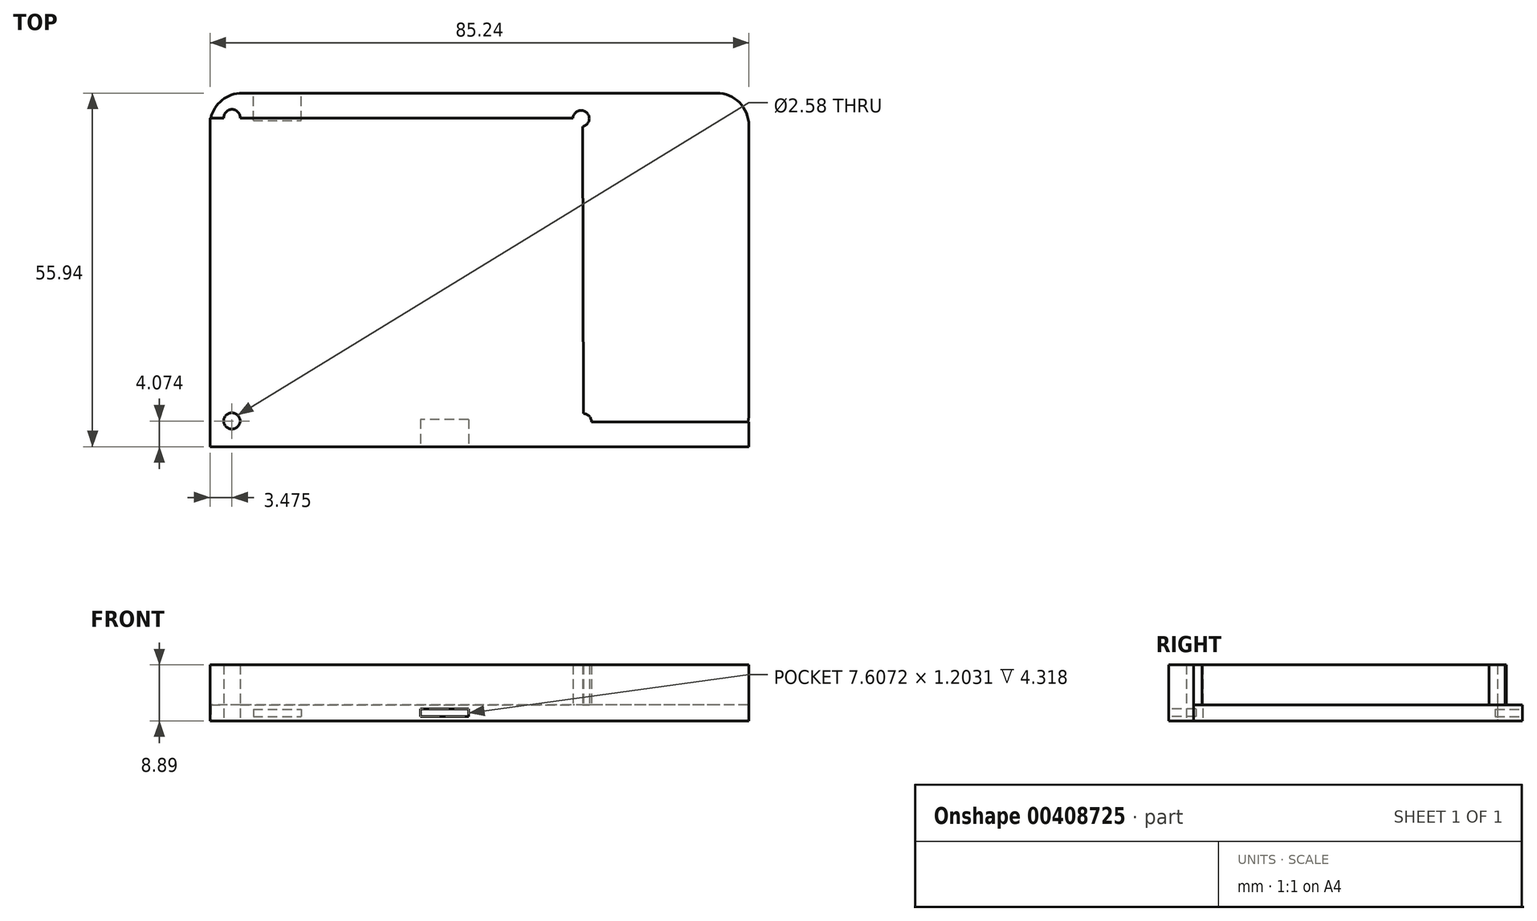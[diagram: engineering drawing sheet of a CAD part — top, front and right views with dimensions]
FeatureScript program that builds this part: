
annotation { "Feature Type Name" : "Feature", "Feature Type Description" : "" }
export const myFeature = defineFeature(function(context is Context, id is Id, definition is map)
    precondition{}
    {
        {
            var Q0;
            Q0=qCreatedBy(makeId("Top.planeOp"),FACE);
            var sketch = newSketch(context, id + "F0", { "sketchPlane" : qUnion([Q0])});
            skLineSegment(sketch, "E0.top", {"start": v(-42.62, -24.03) * mm, "end": v(42.62, -24.03) * mm});
            skLineSegment(sketch, "E0.left", {"start": v(-42.62, 24.03) * mm, "end": v(-42.62, -24.03) * mm});
            skLineSegment(sketch, "E0.right", {"start": v(42.62, 24.03) * mm, "end": v(42.62, -24.03) * mm});
            skPoint(sketch, "E0.middle", {"position": v(0, 0) * mm});
            skLineSegment(sketch, "E1", {"start": v(-42.62, 24.03) * mm, "end": v(-42.62, 27.97) * mm});
            skLineSegment(sketch, "E2.bottom", {"start": v(42.62, 27.97) * mm, "end": v(-42.62, 27.97) * mm});
            skLineSegment(sketch, "E2.top", {"start": v(42.62, -27.97) * mm, "end": v(-42.62, -27.97) * mm});
            skLineSegment(sketch, "E2.left", {"start": v(42.62, 27.97) * mm, "end": v(42.62, -27.97) * mm});
            skLineSegment(sketch, "E2.right", {"start": v(-42.62, 27.97) * mm, "end": v(-42.62, -27.97) * mm});
            skLineSegment(sketch, "E3", {"start": v(16.3, 24.03) * mm, "end": v(-42.62, 24.03) * mm});
            skLineSegment(sketch, "E4", {"start": v(16.3, 24.03) * mm, "end": v(16.46, -24.03) * mm});
            skPoint(sketch, "E5", {"position": v(-39.08, 24.03) * mm});
            skPoint(sketch, "E6", {"position": v(-39.08, -24.03) * mm});
            skPoint(sketch, "E7", {"position": v(16.46, -24.03) * mm});
            skCircle(sketch, "E8", {"center": v(16.43, -24.02) * mm, "radius": 1.3 * mm});
            skCircle(sketch, "E9", {"center": v(-39.13, 24.11) * mm, "radius": 1.3 * mm});
            skCircle(sketch, "E10", {"center": v(-39.15, -23.9) * mm, "radius": 1.3 * mm});
            skCircle(sketch, "E11", {"center": v(16.1, 23.95) * mm, "radius": 1.3 * mm});
            skSolve(sketch);
        }
        {
            var Q0;
            {var subQ3=sQuery(id+"F0.wireOp",EDGE,"E2.bottom");Q0=makeQuery(id+"F0.imprint","IMPRINT",FACE,{"disambiguationData":[TD([[makeQuery(id+"F0.imprint","IMPRINT",EDGE,{"derivedFrom":subQ3}),1.0]])]});}
            var Q1;
            {var subQ6=sQuery(id+"F0.wireOp",EDGE,"E0.top");var subQ10=sQuery(id+"F0.wireOp",EDGE,"E2.right");var subQ11=makeQuery(id+"F0.imprint","INTERSECT",VERTEX,{"derivedFrom":[subQ6,subQ10]});Q1=makeQuery(id+"F0.imprint","IMPRINT",FACE,{"disambiguationData":[TD([[makeQuery(id+"F0.imprint","IMPRINT",EDGE,{"disambiguationData":[TD([[subQ11,-1.0]])],"derivedFrom":subQ6}),1.0]])]});}
            var Q2;
            {var subQ0=sQuery(id+"F0.wireOp",EDGE,"E2.top");Q2=makeQuery(id+"F0.imprint","IMPRINT",FACE,{"disambiguationData":[TD([[makeQuery(id+"F0.imprint","IMPRINT",EDGE,{"derivedFrom":subQ0}),-1.0]])]});}
            extrude(context, id + "F1", {"entities" : qUnion([Q0, Q1, Q2]), "depth" : 2.54 * mm});
        }
        {
            var Q0;
            Q0=makeQuery(id+"F1.opExtrude","SWEPT_EDGE",EDGE,{"disambiguationData":[OSD([sQuery(id+"F0.wireOp",EDGE,"E2.top"),sQuery(id+"F0.wireOp",EDGE,"E2.left")])]});
            var Q1;
            Q1=makeQuery(id+"F1.opExtrude","SWEPT_EDGE",EDGE,{"disambiguationData":[OSD([sQuery(id+"F0.wireOp",EDGE,"E2.top"),sQuery(id+"F0.wireOp",EDGE,"E2.right")])]});
            var Q2;
            Q2=makeQuery(id+"F1.opExtrude","SWEPT_EDGE",EDGE,{"disambiguationData":[OSD([sQuery(id+"F0.wireOp",EDGE,"E2.bottom"),sQuery(id+"F0.wireOp",EDGE,"E2.left")])]});
            var Q3;
            Q3=makeQuery(id+"F1.opExtrude","SWEPT_EDGE",EDGE,{"disambiguationData":[OSD([sQuery(id+"F0.wireOp",EDGE,"E2.bottom"),sQuery(id+"F0.wireOp",EDGE,"E2.right")])]});
            fillet(context, id + "F2", {"entities" : qUnion([Q0, Q1, Q2, Q3]), "radius" : 5.08 * mm, "tangentPropagation" : true, "allowEdgeOverflow" : false});
        }
        {
            var Q0;
            {var subQ0=sQuery(id+"F0.wireOp",EDGE,"E9");var subQ1=sQuery(id+"F0.wireOp",EDGE,"E3");var subQ2=makeQuery(id+"F0.imprint","INTERSECT",VERTEX,{"disambiguationData":[OD(0.0)],"derivedFrom":[subQ1,subQ0]});Q0=makeQuery(id+"F0.imprint","IMPRINT",FACE,{"disambiguationData":[TD([[makeQuery(id+"F0.imprint","IMPRINT",EDGE,{"disambiguationData":[TD([[subQ2,-1.0]])],"derivedFrom":subQ1}),-1.0]])]});}
            var Q1;
            {var subQ0=sQuery(id+"F0.wireOp",EDGE,"E9");var subQ1=sQuery(id+"F0.wireOp",EDGE,"E3");var subQ2=makeQuery(id+"F0.imprint","INTERSECT",VERTEX,{"disambiguationData":[OD(0.0)],"derivedFrom":[subQ1,subQ0]});Q1=makeQuery(id+"F0.imprint","IMPRINT",FACE,{"disambiguationData":[TD([[makeQuery(id+"F0.imprint","IMPRINT",EDGE,{"disambiguationData":[TD([[subQ2,-1.0]])],"derivedFrom":subQ1}),1.0]])]});}
            var Q2;
            {var subQ0=sQuery(id+"F0.wireOp",EDGE,"E10");var subQ1=sQuery(id+"F0.wireOp",EDGE,"E0.top");var subQ2=makeQuery(id+"F0.imprint","INTERSECT",VERTEX,{"disambiguationData":[OD(0.0)],"derivedFrom":[subQ1,subQ0]});Q2=makeQuery(id+"F0.imprint","IMPRINT",FACE,{"disambiguationData":[TD([[makeQuery(id+"F0.imprint","IMPRINT",EDGE,{"disambiguationData":[TD([[subQ2,-1.0]])],"derivedFrom":subQ1}),1.0]])]});}
            var Q3;
            {var subQ0=sQuery(id+"F0.wireOp",EDGE,"E10");var subQ1=sQuery(id+"F0.wireOp",EDGE,"E0.top");var subQ2=makeQuery(id+"F0.imprint","INTERSECT",VERTEX,{"disambiguationData":[OD(0.0)],"derivedFrom":[subQ1,subQ0]});Q3=makeQuery(id+"F0.imprint","IMPRINT",FACE,{"disambiguationData":[TD([[makeQuery(id+"F0.imprint","IMPRINT",EDGE,{"disambiguationData":[TD([[subQ2,-1.0]])],"derivedFrom":subQ1}),-1.0]])]});}
            var Q4;
            {var subQ0=sQuery(id+"F0.wireOp",EDGE,"E4");var subQ1=sQuery(id+"F0.wireOp",EDGE,"E3");var subQ2=makeQuery(id+"F0.imprint","INTERSECT",VERTEX,{"derivedFrom":[subQ1,subQ0]});Q4=makeQuery(id+"F0.imprint","IMPRINT",FACE,{"disambiguationData":[TD([[makeQuery(id+"F0.imprint","IMPRINT",EDGE,{"disambiguationData":[TD([[subQ2,-1.0]])],"derivedFrom":subQ1}),-1.0]])]});}
            var Q5;
            {var subQ0=sQuery(id+"F0.wireOp",EDGE,"E4");var subQ1=sQuery(id+"F0.wireOp",EDGE,"E3");var subQ2=makeQuery(id+"F0.imprint","INTERSECT",VERTEX,{"derivedFrom":[subQ1,subQ0]});Q5=makeQuery(id+"F0.imprint","IMPRINT",FACE,{"disambiguationData":[TD([[makeQuery(id+"F0.imprint","IMPRINT",EDGE,{"disambiguationData":[TD([[subQ2,-1.0]])],"derivedFrom":subQ1}),1.0]])]});}
            var Q6;
            {var subQ0=sQuery(id+"F0.wireOp",EDGE,"E4");var subQ1=sQuery(id+"F0.wireOp",EDGE,"E0.top");var subQ2=makeQuery(id+"F0.imprint","INTERSECT",VERTEX,{"derivedFrom":[subQ1,subQ0]});Q6=makeQuery(id+"F0.imprint","IMPRINT",FACE,{"disambiguationData":[TD([[makeQuery(id+"F0.imprint","IMPRINT",EDGE,{"disambiguationData":[TD([[subQ2,-1.0]])],"derivedFrom":subQ1}),1.0]])]});}
            var Q7;
            {var subQ0=sQuery(id+"F0.wireOp",EDGE,"E4");var subQ1=sQuery(id+"F0.wireOp",EDGE,"E0.top");var subQ2=makeQuery(id+"F0.imprint","INTERSECT",VERTEX,{"derivedFrom":[subQ1,subQ0]});Q7=makeQuery(id+"F0.imprint","IMPRINT",FACE,{"disambiguationData":[TD([[makeQuery(id+"F0.imprint","IMPRINT",EDGE,{"disambiguationData":[TD([[subQ2,1.0]])],"derivedFrom":subQ1}),1.0]])]});}
            var Q8;
            {var subQ0=sQuery(id+"F0.wireOp",EDGE,"E0.top");var subQ1=makeQuery(id+"F0.imprint","INTERSECT",VERTEX,{"derivedFrom":[subQ0,sQuery(id+"F0.wireOp",EDGE,"E4")]});Q8=makeQuery(id+"F0.imprint","IMPRINT",FACE,{"disambiguationData":[TD([[makeQuery(id+"F0.imprint","IMPRINT",EDGE,{"disambiguationData":[TD([[subQ1,1.0]])],"derivedFrom":subQ0}),-1.0]])]});}
            extrude(context, id + "F3", {"entities" : qUnion([Q0, Q1, Q2, Q3, Q4, Q5, Q6, Q7, Q8]), "operationType" : NewBodyOperationType.ADD, "depth" : 8.9 * mm});
        }
        {
            var Q0;
            Q0=makeQuery(id+"F1.opExtrude","SWEPT_FACE",FACE,{"disambiguationData":[OSD([sQuery(id+"F0.wireOp",EDGE,"E2.top")])]});
            var sketch = newSketch(context, id + "F4", { "sketchPlane" : qUnion([Q0])});
            skLineSegment(sketch, "E12", {"start": v(-37.54, 1.27) * mm, "end": v(-5.5, 1.27) * mm});
            skPoint(sketch, "E12.endSnap0", {"position": v(-37.54, 1.27) * mm});
            skSolve(sketch);
        }
        {
            var Q0;
            {var subQ0=sQuery(id+"F0.wireOp",EDGE,"E2.top");var subQ1=makeQuery(id+"F1.opExtrude","CAP_EDGE",EDGE,{"disambiguationData":[OSD([subQ0])],"isStart":true});Q0=makeQuery(id+"F4.imprint","IMPRINT",FACE,{"disambiguationData":[TD([[makeQuery(id+"F4.imprint","IMPRINT",EDGE,{"derivedFrom":subQ1}),-1.0]])]});}
            var sketch = newSketch(context, id + "F5", { "sketchPlane" : qUnion([Q0])});
            skPoint(sketch, "E13", {"position": v(-5.51, 1.29) * mm});
            skLineSegment(sketch, "E14.bottom", {"start": v(-1.7, 1.89) * mm, "end": v(-9.31, 1.89) * mm});
            skLineSegment(sketch, "E14.top", {"start": v(-1.7, 0.68) * mm, "end": v(-9.31, 0.68) * mm});
            skLineSegment(sketch, "E14.left", {"start": v(-1.7, 1.89) * mm, "end": v(-1.7, 0.68) * mm});
            skLineSegment(sketch, "E14.right", {"start": v(-9.31, 1.89) * mm, "end": v(-9.31, 0.68) * mm});
            skSolve(sketch);
        }
        {
            var Q0;
            Q0 = qSketchRegion(id + "F5", true);
            extrude(context, id + "F6", {"entities" : qUnion([Q0]), "operationType" : NewBodyOperationType.REMOVE, "oppositeDirection" : true, "depth" : 4.32 * mm});
        }
        {
            var Q0;
            Q0=makeQuery(id+"F1.opExtrude","SWEPT_FACE",FACE,{"disambiguationData":[OSD([sQuery(id+"F0.wireOp",EDGE,"E2.bottom")])]});
            var sketch = newSketch(context, id + "F7", { "sketchPlane" : qUnion([Q0])});
            skLineSegment(sketch, "E15", {"start": v(39.09, 0) * mm, "end": v(39.09, 1.27) * mm});
            skPoint(sketch, "E15.endSnap0", {"position": v(37.54, 1.27) * mm});
            skLineSegment(sketch, "E16.bottom", {"start": v(35.76, 1.86) * mm, "end": v(28.17, 1.86) * mm});
            skLineSegment(sketch, "E16.top", {"start": v(35.76, 0.68) * mm, "end": v(28.17, 0.68) * mm});
            skLineSegment(sketch, "E16.left", {"start": v(35.76, 1.86) * mm, "end": v(35.76, 0.68) * mm});
            skLineSegment(sketch, "E16.right", {"start": v(28.17, 1.86) * mm, "end": v(28.17, 0.68) * mm});
            skPoint(sketch, "E16.middle", {"position": v(31.96, 1.27) * mm});
            skSolve(sketch);
        }
        {
            var Q0;
            Q0=makeQuery(id+"F7.imprint","IMPRINT",FACE,{"disambiguationData":[TD([[makeQuery(id+"F7.imprint","IMPRINT",EDGE,{"derivedFrom":sQuery(id+"F7.wireOp",EDGE,"E16.bottom")}),1.0]])]});
            extrude(context, id + "F8", {"entities" : qUnion([Q0]), "operationType" : NewBodyOperationType.REMOVE, "oppositeDirection" : true, "depth" : 4.32 * mm});
        }
    });
